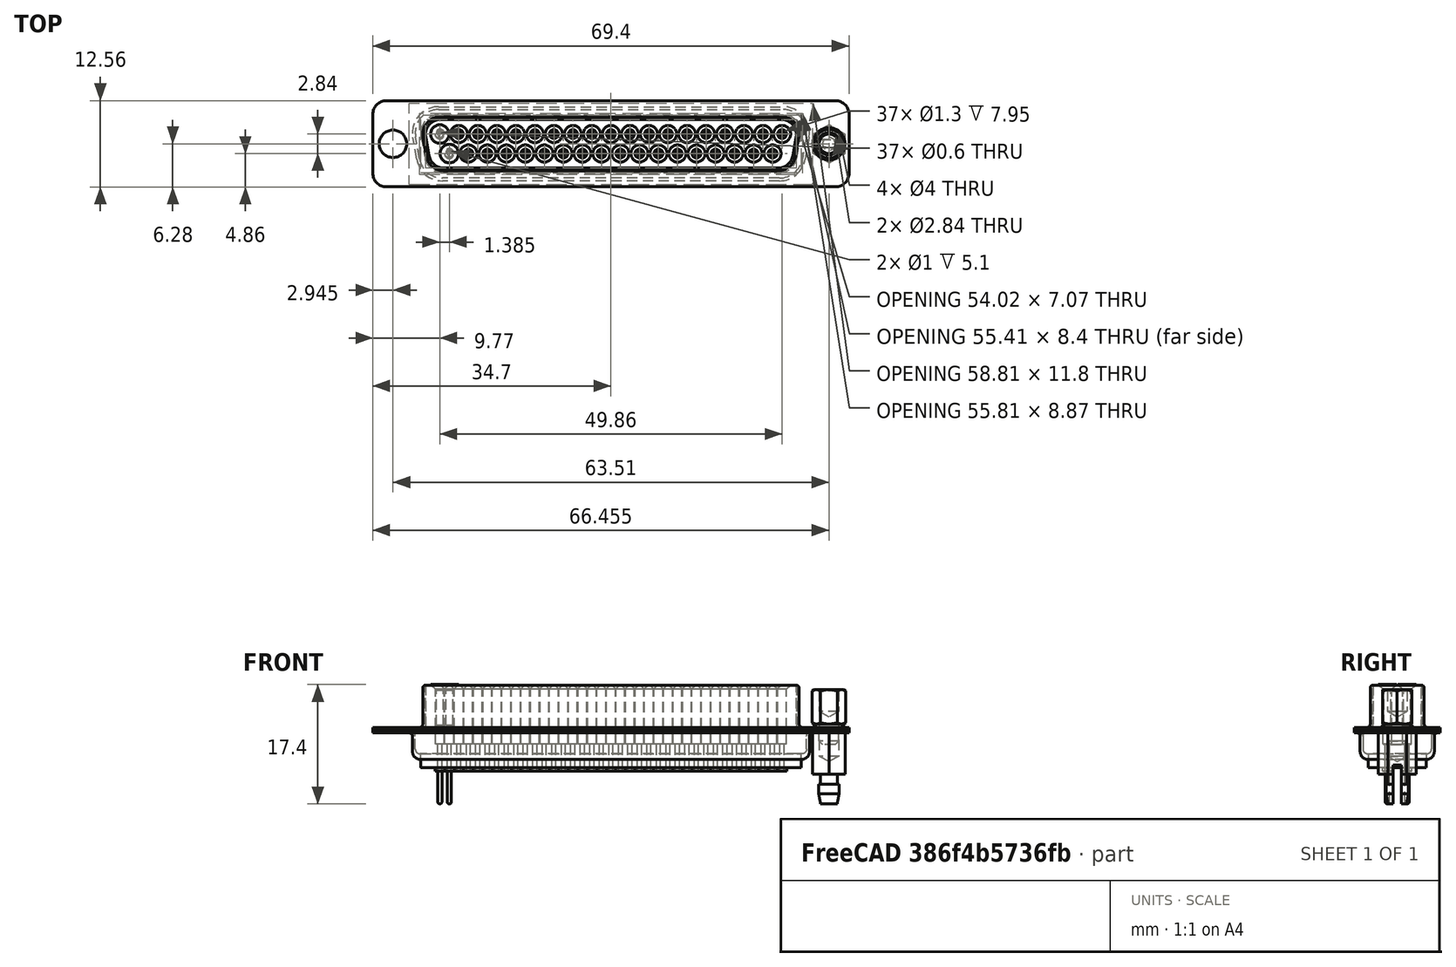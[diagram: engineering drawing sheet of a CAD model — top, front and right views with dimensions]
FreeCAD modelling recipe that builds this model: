
FCSTD DOCUMENT  (FreeCAD 1.0R39319 (Git))
Label: DB 37 Female
License: All rights reserved
LicenseURL: http://en.wikipedia.org/wiki/All_rights_reserved
objects: Sketcher::SketchObject×23, PartDesign::Body×13, PartDesign::Pad×9, PartDesign::Pocket×8, PartDesign::Fillet×8, PartDesign::Revolution×6, Part::FeaturePython×6, Part::MultiFuse×3, PartDesign::FeatureBase×2, PartDesign::Chamfer×1, Part::Cut×1
note: 163 computed .brp shape members not serialized (recipe doc carries the construction recipe); baked Part::Feature solids carry a one-line shape summary decoded from their .brp

FEATURE [Sketcher::SketchObject] Sketch
  ArcFitTolerance = 0
  AttachmentSupport = -> [XY_Plane]
  FullyConstrained = true
  MakeInternals = false
  MapMode = 5
  sketch-geometry (8):
    g0: LineSegment StartX=-32.7 StartY=6.275 StartZ=0 EndX=32.7 EndY=6.275 EndZ=0
    g1: LineSegment StartX=34.7 StartY=4.275 StartZ=0 EndX=34.7 EndY=-4.275 EndZ=0
    g2: LineSegment StartX=32.7 StartY=-6.275 StartZ=0 EndX=-32.7 EndY=-6.275 EndZ=0
    g3: LineSegment StartX=-34.7 StartY=-4.275 StartZ=0 EndX=-34.7 EndY=4.275 EndZ=0
    g4: ArcOfCircle CenterX=-32.7 CenterY=4.275 CenterZ=0 NormalX=0 NormalY=0 NormalZ=1 AngleXU=0 Radius=2 StartAngle=1.5708 EndAngle=3.14159
    g5: ArcOfCircle CenterX=-32.7 CenterY=-4.275 CenterZ=0 NormalX=0 NormalY=0 NormalZ=1 AngleXU=0 Radius=2 StartAngle=3.14159 EndAngle=4.71239
    g6: ArcOfCircle CenterX=32.7 CenterY=4.275 CenterZ=0 NormalX=0 NormalY=0 NormalZ=1 AngleXU=0 Radius=2 StartAngle=0 EndAngle=1.5708
    g7: ArcOfCircle CenterX=32.7 CenterY=-4.275 CenterZ=0 NormalX=0 NormalY=0 NormalZ=1 AngleXU=0 Radius=2 StartAngle=4.71239 EndAngle=6.28319
  constraints (19):
    c: Horizontal(g0)
    c: Horizontal(g2)
    c: Vertical(g1)
    c: Vertical(g3)
    c: Tangent(g0,g4) = 1.5708
    c: Tangent(g3,g4) = 1.5708
    c: Tangent(g3,g5) = 1.5708
    c: Tangent(g2,g5) = 1.5708
    c: Tangent(g0,g6) = 1.5708
    c: Tangent(g1,g6) = 1.5708
    c: Tangent(g1,g7) = 1.5708
    c: Tangent(g2,g7) = 1.5708
    c: Equal(g7,g6)
    c: Equal(g6,g4)
    c: Equal(g4,g5)
    c: Symmetric(g4,g7,g-1)
    c: Radius(g4) = 2
    c: DistanceY(g2,g0) = 12.55
    c: DistanceX(g3,g1) = 69.4
FEATURE [PartDesign::Pad] Pad
  Direction = (0,0,1)
  Length = 0.4
  Length2 = 10
  Profile = -> Sketch
  ReferenceAxis = -> Sketch [N_Axis]
  Suppressed = false
  Type = 0
FEATURE [Sketcher::SketchObject] Sketch001
  ArcFitTolerance = 0
  AttachmentSupport = -> [Pad]
  FullyConstrained = true
  MakeInternals = false
  MapMode = 5
  Placement = pos=(0,0,0.4) rot=(0,0,1;0rad)
  sketch-geometry (2):
    g0: Circle CenterX=-31.755 CenterY=0 CenterZ=0 NormalX=0 NormalY=0 NormalZ=1 AngleXU=0 Radius=2
    g1: Circle CenterX=31.755 CenterY=0 CenterZ=0 NormalX=0 NormalY=0 NormalZ=1 AngleXU=0 Radius=2
  constraints (5):
    c: PointOnObject(g0,g-1)
    c: Symmetric(g1,g0,g-2)
    c: Equal(g1,g0)
    c: DistanceX(g0,g1) = 63.51
    c: Diameter(g0) = 4
FEATURE [PartDesign::Pocket] Pocket
  BaseFeature = -> Pad
  Direction = (0,0,-1)
  Length = 5
  Length2 = 5
  Profile = -> Sketch001
  ReferenceAxis = -> Sketch001 [N_Axis]
  Suppressed = false
  Type = 0
FEATURE [Sketcher::SketchObject] Sketch002
  ArcFitTolerance = 0
  AttachmentSupport = -> [Pocket]
  FullyConstrained = true
  MakeInternals = false
  MapMode = 5
  Placement = pos=(0,0,0.4) rot=(0,0,1;0rad)
  sketch-geometry (10):
    g0: LineSegment StartX=-24.865 StartY=3.935 StartZ=0 EndX=24.865 EndY=3.935 EndZ=0
    g1: LineSegment StartX=27.3714 StartY=0.948231 StartZ=0 EndX=26.8814 EndY=-1.83177 EndZ=0
    g2: LineSegment StartX=24.375 StartY=-3.935 StartZ=0 EndX=-24.375 EndY=-3.935 EndZ=0
    g3: LineSegment StartX=-26.8814 StartY=-1.83177 StartZ=0 EndX=-27.3714 EndY=0.948231 EndZ=0
    g4: ArcOfCircle CenterX=-24.865 CenterY=1.39 CenterZ=0 NormalX=0 NormalY=0 NormalZ=1 AngleXU=0 Radius=2.545 StartAngle=1.5708 EndAngle=3.31606
    g5: ArcOfCircle CenterX=-24.375 CenterY=-1.39 CenterZ=0 NormalX=0 NormalY=0 NormalZ=1 AngleXU=0 Radius=2.545 StartAngle=3.31606 EndAngle=4.71239
    g6: ArcOfCircle CenterX=24.375 CenterY=-1.39 CenterZ=0 NormalX=0 NormalY=0 NormalZ=1 AngleXU=0 Radius=2.545 StartAngle=4.71239 EndAngle=6.10872
    g7: ArcOfCircle CenterX=24.865 CenterY=1.39 CenterZ=0 NormalX=0 NormalY=0 NormalZ=1 AngleXU=0 Radius=2.545 StartAngle=6.10872 EndAngle=7.85398
    g8: LineSegment [constr] StartX=-24.865 StartY=3.935 StartZ=0 EndX=-24.865 EndY=0 EndZ=0
    g9: LineSegment [constr] StartX=-24.375 StartY=-3.935 StartZ=0 EndX=-24.375 EndY=0 EndZ=0
  constraints (24):
    c: Tangent(g0,g4) = 1.5708
    c: Tangent(g3,g4) = 1.5708
    c: Tangent(g3,g5) = 1.5708
    c: Tangent(g2,g5) = 1.5708
    c: Tangent(g2,g6) = 1.5708
    c: Tangent(g1,g6) = 1.5708
    c: Tangent(g1,g7) = 1.5708
    c: Tangent(g0,g7) = 1.5708
    c: Symmetric(g4,g7,g-2)
    c: Equal(g4,g5)
    c: Equal(g5,g7)
    c: Equal(g7,g6)
    c: Symmetric(g5,g6,g-2)
    c: Coincident(g8,g0)
    c: PointOnObject(g8,g-1)
    c: Vertical(g8)
    c: Coincident(g9,g2)
    c: PointOnObject(g9,g-1)
    c: Vertical(g9)
    c: Equal(g9,g8)
    c: DistanceY(g2,g0) = 7.87
    c: DistanceX(g0,g0) = 49.73
    c: DistanceX(g2,g2) = 48.75
    c: Radius(g4) = 2.545
FEATURE [PartDesign::Pad] Pad001
  BaseFeature = -> Pocket
  Direction = (0,0,1)
  Length = 6.15
  Length2 = 10
  Profile = -> Sketch002
  ReferenceAxis = -> Sketch002 [N_Axis]
  Suppressed = false
  Type = 0
FEATURE [Sketcher::SketchObject] Sketch003
  ArcFitTolerance = 0
  AttachmentSupport = -> [Pad001]
  ExternalGeometry = -> [Pad001]
  FullyConstrained = true
  MakeInternals = false
  MapMode = 5
  Placement = pos=(0,0,6.55) rot=(0,0,1;0rad)
  sketch-geometry (8):
    g0: LineSegment StartX=-24.865 StartY=3.535 StartZ=0 EndX=24.865 EndY=3.535 EndZ=0
    g1: LineSegment StartX=26.9774 StartY=1.01766 StartZ=0 EndX=26.4874 EndY=-1.76234 EndZ=0
    g2: LineSegment StartX=24.375 StartY=-3.535 StartZ=0 EndX=-24.375 EndY=-3.535 EndZ=0
    g3: LineSegment StartX=-26.4874 StartY=-1.76234 StartZ=0 EndX=-26.9774 EndY=1.01766 EndZ=0
    g4: ArcOfCircle CenterX=-24.865 CenterY=1.39 CenterZ=0 NormalX=0 NormalY=0 NormalZ=1 AngleXU=0 Radius=2.145 StartAngle=1.5708 EndAngle=3.31606
    g5: ArcOfCircle CenterX=24.865 CenterY=1.39 CenterZ=0 NormalX=0 NormalY=0 NormalZ=1 AngleXU=0 Radius=2.145 StartAngle=6.10872 EndAngle=7.85398
    g6: ArcOfCircle CenterX=24.375 CenterY=-1.39 CenterZ=0 NormalX=0 NormalY=0 NormalZ=1 AngleXU=0 Radius=2.145 StartAngle=4.71239 EndAngle=6.10872
    g7: ArcOfCircle CenterX=-24.375 CenterY=-1.39 CenterZ=0 NormalX=0 NormalY=0 NormalZ=1 AngleXU=0 Radius=2.145 StartAngle=3.31606 EndAngle=4.71239
  constraints (16):
    c: Tangent(g0,g4) = 1.5708
    c: Tangent(g3,g4) = 1.5708
    c: Tangent(g0,g5) = 1.5708
    c: Tangent(g1,g5) = 1.5708
    c: Tangent(g2,g6) = 1.5708
    c: Tangent(g1,g6) = 1.5708
    c: Tangent(g3,g7) = 1.5708
    c: Tangent(g2,g7) = 1.5708
    c: Equal(g4,g7)
    c: Equal(g7,g5)
    c: Equal(g5,g6)
    c: Coincident(g6,g-6)
    c: Coincident(g5,g-5)
    c: Coincident(g4,g-3)
    c: Coincident(g7,g-4)
    c: DistanceY(g0,g-3) = 0.4
FEATURE [PartDesign::Pocket] Pocket001
  BaseFeature = -> Pad001
  Direction = (0,0,-1)
  Length = 5
  Length2 = 5
  Profile = -> Sketch003
  ReferenceAxis = -> Sketch003 [N_Axis]
  Suppressed = false
  Type = 1
FEATURE [PartDesign::Fillet] Fillet
  Base = -> Pocket001 [Edge33]
  BaseFeature = -> Pocket001
  Radius = 0.5
  SupportTransform = false
  Suppressed = false
  UseAllEdges = false
FEATURE [PartDesign::Fillet] Fillet001
  Base = -> Fillet [Edge61]
  BaseFeature = -> Fillet
  Radius = 0.39
  SupportTransform = false
  Suppressed = false
  UseAllEdges = false
FEATURE [PartDesign::Fillet] Fillet002
  Base = -> Fillet001 [Edge80]
  BaseFeature = -> Fillet001
  Radius = 0.9
  SupportTransform = false
  Suppressed = false
  UseAllEdges = false
FEATURE [PartDesign::Body] Body
  AllowCompound = false
  Group = -> [Sketch,Pad,Sketch001,Pocket,Sketch002,Sketch003,Pad001,Pocket001,Fillet,Fillet001,Fillet002]
  Origin = -> Origin
  Tip = -> Fillet002
FEATURE [Sketcher::SketchObject] Sketch004
  ArcFitTolerance = 0
  AttachmentSupport = -> [XY_Plane001]
  FullyConstrained = true
  MakeInternals = false
  MapMode = 5
  sketch-geometry (8):
    g0: LineSegment StartX=-32.7 StartY=6.275 StartZ=0 EndX=32.7 EndY=6.275 EndZ=0
    g1: LineSegment StartX=34.7 StartY=4.275 StartZ=0 EndX=34.7 EndY=-4.275 EndZ=0
    g2: LineSegment StartX=32.7 StartY=-6.275 StartZ=0 EndX=-32.7 EndY=-6.275 EndZ=0
    g3: LineSegment StartX=-34.7 StartY=-4.275 StartZ=0 EndX=-34.7 EndY=4.275 EndZ=0
    g4: ArcOfCircle CenterX=-32.7 CenterY=4.275 CenterZ=0 NormalX=0 NormalY=0 NormalZ=1 AngleXU=0 Radius=2 StartAngle=1.5708 EndAngle=3.14159
    g5: ArcOfCircle CenterX=-32.7 CenterY=-4.275 CenterZ=0 NormalX=0 NormalY=0 NormalZ=1 AngleXU=0 Radius=2 StartAngle=3.14159 EndAngle=4.71239
    g6: ArcOfCircle CenterX=32.7 CenterY=4.275 CenterZ=0 NormalX=0 NormalY=0 NormalZ=1 AngleXU=0 Radius=2 StartAngle=0 EndAngle=1.5708
    g7: ArcOfCircle CenterX=32.7 CenterY=-4.275 CenterZ=0 NormalX=0 NormalY=0 NormalZ=1 AngleXU=0 Radius=2 StartAngle=4.71239 EndAngle=6.28319
  constraints (19):
    c: Horizontal(g0)
    c: Horizontal(g2)
    c: Vertical(g1)
    c: Vertical(g3)
    c: Tangent(g0,g4) = 1.5708
    c: Tangent(g3,g4) = 1.5708
    c: Tangent(g3,g5) = 1.5708
    c: Tangent(g2,g5) = 1.5708
    c: Tangent(g0,g6) = 1.5708
    c: Tangent(g1,g6) = 1.5708
    c: Tangent(g1,g7) = 1.5708
    c: Tangent(g2,g7) = 1.5708
    c: Equal(g7,g6)
    c: Equal(g6,g4)
    c: Equal(g4,g5)
    c: Symmetric(g4,g7,g-1)
    c: Radius(g4) = 2
    c: DistanceY(g2,g0) = 12.55
    c: DistanceX(g3,g1) = 69.4
FEATURE [PartDesign::Pad] Pad002
  Direction = (0,0,1)
  Length = 0.4
  Length2 = 10
  Profile = -> Sketch004
  ReferenceAxis = -> Sketch004 [N_Axis]
  Suppressed = false
  Type = 0
FEATURE [Sketcher::SketchObject] Sketch005
  ArcFitTolerance = 0
  AttachmentSupport = -> [Pad002]
  FullyConstrained = true
  MakeInternals = false
  MapMode = 5
  Placement = pos=(0,0,0.4) rot=(0,0,1;0rad)
  sketch-geometry (2):
    g0: Circle CenterX=-31.755 CenterY=0 CenterZ=0 NormalX=0 NormalY=0 NormalZ=1 AngleXU=0 Radius=2
    g1: Circle CenterX=31.755 CenterY=0 CenterZ=0 NormalX=0 NormalY=0 NormalZ=1 AngleXU=0 Radius=2
  constraints (5):
    c: PointOnObject(g0,g-1)
    c: Symmetric(g1,g0,g-2)
    c: Equal(g1,g0)
    c: DistanceX(g0,g1) = 63.51
    c: Diameter(g0) = 4
FEATURE [PartDesign::Pocket] Pocket002
  BaseFeature = -> Pad002
  Direction = (0,0,-1)
  Length = 5
  Length2 = 5
  Profile = -> Sketch005
  ReferenceAxis = -> Sketch005 [N_Axis]
  Suppressed = false
  Type = 0
FEATURE [Sketcher::SketchObject] Sketch006
  ArcFitTolerance = 0
  AttachmentSupport = -> [Pocket002]
  FullyConstrained = true
  MakeInternals = false
  MapMode = 5
  Placement = pos=(0,0,0.4) rot=(0,0,1;0rad)
  sketch-geometry (10):
    g0: LineSegment StartX=-25.11 StartY=5.4 StartZ=0 EndX=25.11 EndY=5.4 EndZ=0
    g1: LineSegment StartX=28.8521 StartY=0.939282 StartZ=0 EndX=28.2871 EndY=-2.26072 EndZ=0
    g2: LineSegment StartX=24.545 StartY=-5.4 StartZ=0 EndX=-24.545 EndY=-5.4 EndZ=0
    g3: LineSegment StartX=-28.2871 StartY=-2.26072 StartZ=0 EndX=-28.8521 EndY=0.939282 EndZ=0
    g4: ArcOfCircle CenterX=-25.11 CenterY=1.6 CenterZ=0 NormalX=0 NormalY=0 NormalZ=1 AngleXU=0 Radius=3.8 StartAngle=1.5708 EndAngle=3.31635
    g5: ArcOfCircle CenterX=-24.545 CenterY=-1.6 CenterZ=0 NormalX=0 NormalY=0 NormalZ=1 AngleXU=0 Radius=3.8 StartAngle=3.31635 EndAngle=4.71239
    g6: ArcOfCircle CenterX=24.545 CenterY=-1.6 CenterZ=0 NormalX=0 NormalY=0 NormalZ=1 AngleXU=0 Radius=3.8 StartAngle=4.71239 EndAngle=6.10842
    g7: ArcOfCircle CenterX=25.11 CenterY=1.6 CenterZ=0 NormalX=0 NormalY=0 NormalZ=1 AngleXU=0 Radius=3.8 StartAngle=6.10842 EndAngle=7.85398
    g8: LineSegment [constr] StartX=-25.11 StartY=5.4 StartZ=0 EndX=-25.11 EndY=0 EndZ=0
    g9: LineSegment [constr] StartX=-24.545 StartY=-5.4 StartZ=0 EndX=-24.545 EndY=0 EndZ=0
  constraints (24):
    c: Tangent(g0,g4) = 1.5708
    c: Tangent(g3,g4) = 1.5708
    c: Tangent(g3,g5) = 1.5708
    c: Tangent(g2,g5) = 1.5708
    c: Tangent(g2,g6) = 1.5708
    c: Tangent(g1,g6) = 1.5708
    c: Tangent(g1,g7) = 1.5708
    c: Tangent(g0,g7) = 1.5708
    c: Symmetric(g4,g7,g-2)
    c: Equal(g4,g5)
    c: Equal(g5,g7)
    c: Equal(g7,g6)
    c: Symmetric(g5,g6,g-2)
    c: DistanceX(g0,g0) = 50.22
    c: DistanceX(g2,g2) = 49.09
    c: Coincident(g8,g0)
    c: PointOnObject(g8,g-1)
    c: Vertical(g8)
    c: Coincident(g9,g2)
    c: PointOnObject(g9,g-1)
    c: Vertical(g9)
    c: Equal(g9,g8)
    c: DistanceY(g2,g0) = 10.8
    c: Radius(g4) = 3.8
FEATURE [PartDesign::Pad] Pad003
  BaseFeature = -> Pocket002
  Direction = (0,0,1)
  Length = 3.85
  Length2 = 10
  Profile = -> Sketch006
  ReferenceAxis = -> Sketch006 [N_Axis]
  Suppressed = false
  Type = 0
FEATURE [Sketcher::SketchObject] Sketch007
  ArcFitTolerance = 0
  AttachmentSupport = -> [Pad003]
  ExternalGeometry = -> [Pad003]
  FullyConstrained = true
  MakeInternals = false
  MapMode = 5
  Placement = pos=(0,0,4.25) rot=(0,0,1;0rad)
  sketch-geometry (8):
    g0: LineSegment StartX=-25.11 StartY=4.2 StartZ=0 EndX=25.11 EndY=4.2 EndZ=0
    g1: LineSegment StartX=27.6704 StartY=1.14793 StartZ=0 EndX=27.1054 EndY=-2.05207 EndZ=0
    g2: LineSegment StartX=24.545 StartY=-4.2 StartZ=0 EndX=-24.545 EndY=-4.2 EndZ=0
    g3: LineSegment StartX=-27.1054 StartY=-2.05207 StartZ=0 EndX=-27.6704 EndY=1.14793 EndZ=0
    g4: ArcOfCircle CenterX=-25.11 CenterY=1.6 CenterZ=0 NormalX=0 NormalY=0 NormalZ=1 AngleXU=0 Radius=2.6 StartAngle=1.5708 EndAngle=3.31635
    g5: ArcOfCircle CenterX=25.11 CenterY=1.6 CenterZ=0 NormalX=0 NormalY=0 NormalZ=1 AngleXU=0 Radius=2.6 StartAngle=6.10842 EndAngle=7.85398
    g6: ArcOfCircle CenterX=24.545 CenterY=-1.6 CenterZ=0 NormalX=0 NormalY=0 NormalZ=1 AngleXU=0 Radius=2.6 StartAngle=4.71239 EndAngle=6.10842
    g7: ArcOfCircle CenterX=-24.545 CenterY=-1.6 CenterZ=0 NormalX=0 NormalY=0 NormalZ=1 AngleXU=0 Radius=2.6 StartAngle=3.31635 EndAngle=4.71239
  constraints (20):
    c: Tangent(g0,g4) = 1.5708
    c: Tangent(g3,g4) = 1.5708
    c: Tangent(g0,g5) = 1.5708
    c: Tangent(g1,g5) = 1.5708
    c: Tangent(g2,g6) = 1.5708
    c: Tangent(g1,g6) = 1.5708
    c: Tangent(g3,g7) = 1.5708
    c: Tangent(g2,g7) = 1.5708
    c: Equal(g4,g7)
    c: Equal(g7,g5)
    c: Equal(g5,g6)
    c: Coincident(g6,g-6)
    c: Coincident(g5,g-5)
    c: Coincident(g4,g-3)
    c: Coincident(g7,g-4)
    c: DistanceY(g0,g-3) = 1.2
    c: Radius(g4) = 2.6
    c: DistanceY(g2,g0) = 8.4
    c: DistanceX(g0,g0) = 50.22
    c: DistanceX(g2,g2) = 49.09
FEATURE [PartDesign::Pocket] Pocket003
  BaseFeature = -> Pad003
  Direction = (0,0,-1)
  Length = 5
  Length2 = 5
  Profile = -> Sketch007
  ReferenceAxis = -> Sketch007 [N_Axis]
  Suppressed = false
  Type = 1
FEATURE [Sketcher::SketchObject] Sketch008
  ArcFitTolerance = 0
  AttachmentSupport = -> [Pocket003]
  ExternalGeometry = -> [Pocket003]
  FullyConstrained = true
  MakeInternals = false
  MapMode = 5
  Placement = pos=(0,0,0) rot=(1,0,0;3.14159rad)
  sketch-geometry (8):
    g0: LineSegment StartX=-24.545 StartY=5 StartZ=0 EndX=24.545 EndY=5 EndZ=0
    g1: LineSegment StartX=27.8932 StartY=2.19117 StartZ=0 EndX=28.4582 EndY=-1.00883 EndZ=0
    g2: LineSegment StartX=25.11 StartY=-5 StartZ=0 EndX=-25.11 EndY=-5 EndZ=0
    g3: LineSegment StartX=-28.4582 StartY=-1.00883 StartZ=0 EndX=-27.8932 EndY=2.19117 EndZ=0
    g4: ArcOfCircle CenterX=-24.545 CenterY=1.6 CenterZ=0 NormalX=0 NormalY=0 NormalZ=1 AngleXU=0 Radius=3.4 StartAngle=1.5708 EndAngle=2.96683
    g5: ArcOfCircle CenterX=-25.11 CenterY=-1.6 CenterZ=0 NormalX=0 NormalY=0 NormalZ=1 AngleXU=0 Radius=3.4 StartAngle=2.96683 EndAngle=4.71239
    g6: ArcOfCircle CenterX=25.11 CenterY=-1.6 CenterZ=0 NormalX=0 NormalY=0 NormalZ=1 AngleXU=0 Radius=3.4 StartAngle=4.71239 EndAngle=6.45795
    g7: ArcOfCircle CenterX=24.545 CenterY=1.6 CenterZ=0 NormalX=0 NormalY=0 NormalZ=1 AngleXU=0 Radius=3.4 StartAngle=0.174761 EndAngle=1.5708
  constraints (16):
    c: Tangent(g0,g4) = 1.5708
    c: Tangent(g3,g4) = 1.5708
    c: Tangent(g3,g5) = 1.5708
    c: Tangent(g2,g5) = 1.5708
    c: Tangent(g2,g6) = 1.5708
    c: Tangent(g1,g6) = 1.5708
    c: Tangent(g1,g7) = 1.5708
    c: Tangent(g0,g7) = 1.5708
    c: Coincident(g-3,g4)
    c: Coincident(g5,g-4)
    c: Coincident(g-6,g7)
    c: Coincident(g-5,g6)
    c: Equal(g5,g4)
    c: Equal(g4,g7)
    c: Equal(g7,g6)
    c: DistanceY(g-3,g0) = 0.8
FEATURE [PartDesign::Pocket] Pocket004
  BaseFeature = -> Pocket003
  Direction = (0,0,1)
  Length = 3.45
  Length2 = 5
  Profile = -> Sketch008
  ReferenceAxis = -> Sketch008 [N_Axis]
  Suppressed = false
  Type = 0
FEATURE [PartDesign::Fillet] Fillet003
  Base = -> Pocket004 [Edge58]
  BaseFeature = -> Pocket004
  Radius = 0.7
  SupportTransform = false
  Suppressed = false
  UseAllEdges = false
FEATURE [PartDesign::Fillet] Fillet004
  Base = -> Fillet003 [Edge99]
  BaseFeature = -> Fillet003
  Radius = 0.5
  SupportTransform = false
  Suppressed = false
  UseAllEdges = false
FEATURE [PartDesign::Fillet] Fillet005
  Base = -> Fillet004 [Edge56]
  BaseFeature = -> Fillet004
  Radius = 1.1
  SupportTransform = false
  Suppressed = false
  UseAllEdges = false
FEATURE [PartDesign::Fillet] Fillet006
  Base = -> Fillet005 [Edge125]
  BaseFeature = -> Fillet005
  Radius = 0.9
  SupportTransform = false
  Suppressed = false
  UseAllEdges = false
FEATURE [PartDesign::Body] Body001
  AllowCompound = false
  Group = -> [Sketch004,Pad002,Sketch005,Pocket002,Sketch006,Sketch007,Pad003,Pocket003,Sketch008,Pocket004,Fillet003,Fillet004,Fillet005,Fillet006]
  Origin = -> Origin001
  Placement = pos=(0,0,0) rot=(0,1,0;3.14159rad)
  Tip = -> Fillet006
FEATURE [Sketcher::SketchObject] Sketch009
  ArcFitTolerance = 0
  AttachmentSupport = -> [XZ_Plane002]
  FullyConstrained = true
  MakeInternals = false
  MapMode = 5
  Placement = pos=(0,0,0) rot=(1,0,0;1.5708rad)
  sketch-geometry (14):
    g0: LineSegment StartX=1.4224 StartY=0.5 StartZ=0 EndX=1.4224 EndY=-4.17878 EndZ=0
    g1: LineSegment StartX=1.4224 StartY=-4.17878 StartZ=0 EndX=0 EndY=-5 EndZ=0
    g2: LineSegment StartX=0 StartY=-5 StartZ=0 EndX=0 EndY=-11.1 EndZ=0
    g3: LineSegment StartX=0 StartY=-11.1 StartZ=0 EndX=1.35 EndY=-11.1 EndZ=0
    g4: LineSegment StartX=1.35 StartY=-11.1 StartZ=0 EndX=1.6 EndY=-9.7 EndZ=0
    g5: LineSegment StartX=1.6 StartY=-9.7 StartZ=0 EndX=1.6 EndY=-8.3 EndZ=0
    g6: LineSegment StartX=1.6 StartY=-8.3 StartZ=0 EndX=1.4 EndY=-8.3 EndZ=0
    g7: LineSegment StartX=1.4 StartY=-8.3 StartZ=0 EndX=1.4 EndY=-6.8 EndZ=0
    g8: LineSegment StartX=1.4 StartY=-6.8 StartZ=0 EndX=4 EndY=-6.8 EndZ=0
    g9: LineSegment StartX=4 StartY=-6.8 StartZ=0 EndX=4 EndY=-0.8 EndZ=0
    g10: LineSegment StartX=4 StartY=-0.8 StartZ=0 EndX=2 EndY=-0.8 EndZ=0
    g11: LineSegment StartX=2 StartY=-0.8 StartZ=0 EndX=2 EndY=0 EndZ=0
    g12: LineSegment StartX=2 StartY=0 StartZ=0 EndX=2.35 EndY=-9.64e-14 EndZ=0
    g13: ArcOfCircle CenterX=1.4224 CenterY=-0.610442 CenterZ=0 NormalX=0 NormalY=0 NormalZ=1 AngleXU=0 Radius=1.11044 StartAngle=0.582039 EndAngle=1.5708
  constraints (43):
    c: Vertical(g0)
    c: Coincident(g0,g1)
    c: Coincident(g1,g2)
    c: Vertical(g2)
    c: Coincident(g2,g3)
    c: Coincident(g3,g4)
    c: Coincident(g4,g5)
    c: Vertical(g5)
    c: Coincident(g5,g6)
    c: Horizontal(g6)
    c: Coincident(g6,g7)
    c: Vertical(g7)
    c: Coincident(g7,g8)
    c: Coincident(g8,g9)
    c: Vertical(g9)
    c: Coincident(g9,g10)
    c: Horizontal(g10)
    c: Coincident(g10,g11)
    c: PointOnObject(g11,g-1)
    c: Vertical(g11)
    c: Coincident(g11,g12)
    c: PointOnObject(g12,g-1)
    c: Coincident(g13,g12)
    c: Coincident(g13,g0)
    c: PointOnObject(g13,g0)
    c: DistanceX(g-1,g11) = 2
    c: DistanceX(g-1,g0) = 1.4224
    c: DistanceY(g10,g11) = 0.8
    c: Horizontal(g8)
    c: DistanceY(g9,g9) = 6
    c: DistanceY(g3,g9) = 10.3
    c: Horizontal(g3)
    c: DistanceX(g2,g4) = 1.6
    c: PointOnObject(g1,g-2)
    c: DistanceY(g5,g8) = 1.5
    c: DistanceX(g2,g6) = 1.4
    c: DistanceX(g3,g4) = 0.25
    c: DistanceY(g4,g4) = 1.4
    c: DistanceY(g1,g-1) = 5
    c: Angle(g1,g-2) = 1.0472
    c: DistanceX(g12,g12) = 0.35
    c: DistanceY(g11,g0) = 0.5
    c: DistanceX(g-1,g9) = 4
FEATURE [PartDesign::Revolution] Revolution
  Angle = 360
  Angle2 = 60
  Axis = (0,2e-16,1)
  Base = (0,0,0)
  Placement = pos=(0,0,0) rot=(1,0,0;1.5708rad)
  Profile = -> Sketch009
  ReferenceAxis = -> Sketch009 [V_Axis]
  Reversed = true
  Suppressed = false
  Type = 0
FEATURE [Sketcher::SketchObject] Sketch010
  ArcFitTolerance = 0
  AttachmentSupport = -> [Revolution]
  FullyConstrained = false
  MakeInternals = false
  MapMode = 5
  Placement = pos=(0,-2e-16,-0.8) rot=(0,0,1;3.14159rad)
  sketch-geometry (8):
    g0: LineSegment StartX=0 StartY=2.74241 StartZ=0 EndX=-2.375 EndY=1.37121 EndZ=0
    g1: LineSegment StartX=-2.375 StartY=1.37121 StartZ=0 EndX=-2.375 EndY=-1.37121 EndZ=0
    g2: LineSegment StartX=-2.375 StartY=-1.37121 StartZ=0 EndX=-7.545e-13 EndY=-2.74241 EndZ=0
    g3: LineSegment StartX=-7.545e-13 StartY=-2.74241 StartZ=0 EndX=2.375 EndY=-1.37121 EndZ=0
    g4: LineSegment StartX=2.375 StartY=-1.37121 StartZ=0 EndX=2.375 EndY=1.37121 EndZ=0
    g5: LineSegment StartX=2.375 StartY=1.37121 StartZ=0 EndX=0 EndY=2.74241 EndZ=0
    g6: Circle [constr] CenterX=0 CenterY=0 CenterZ=0 NormalX=0 NormalY=0 NormalZ=1 AngleXU=0 Radius=2.74241
    g7: Circle CenterX=0 CenterY=0 CenterZ=0 NormalX=0 NormalY=0 NormalZ=1 AngleXU=0 Radius=4.67961
  constraints (17):
    c: Coincident(g0,g1)
    c: Coincident(g1,g2)
    c: Coincident(g2,g3)
    c: Coincident(g3,g4)
    c: Coincident(g4,g5)
    c: Coincident(g5,g0)
    c: Equal(g0, g1-g5) x5
    c: PointOnObject(g0,g6)
    c: PointOnObject(g1,g6)
    c: PointOnObject(g2,g6)
    c: PointOnObject(g3,g6)
    c: PointOnObject(g4,g6)
    c: PointOnObject(g5,g6)
    c: Coincident(g6,g-1)
    c: PointOnObject(g5,g-2)
    c: DistanceX(g0,g4) = 4.75
    c: Coincident(g7,g6)
FEATURE [PartDesign::Pocket] Pocket005
  BaseFeature = -> Revolution
  Direction = (0,0,-1)
  Length = 5
  Length2 = 5
  Placement = pos=(0,0,0) rot=(1,0,0;1.5708rad)
  Profile = -> Sketch010
  ReferenceAxis = -> Sketch010 [N_Axis]
  Suppressed = false
  Type = 1
FEATURE [Sketcher::SketchObject] Sketch011
  ArcFitTolerance = 0
  AttachmentSupport = -> [YZ_Plane002]
  FullyConstrained = true
  MakeInternals = false
  MapMode = 5
  Placement = pos=(0,0,0) rot=(0.57735,0.57735,0.57735;2.0944rad)
  sketch-geometry (4):
    g0: LineSegment StartX=-0.6 StartY=-5.5 StartZ=0 EndX=0.6 EndY=-5.5 EndZ=0
    g1: LineSegment StartX=0.6 StartY=-5.5 StartZ=0 EndX=0.6 EndY=-11.5 EndZ=0
    g2: LineSegment StartX=0.6 StartY=-11.5 StartZ=0 EndX=-0.6 EndY=-11.5 EndZ=0
    g3: LineSegment StartX=-0.6 StartY=-11.5 StartZ=0 EndX=-0.6 EndY=-5.5 EndZ=0
  constraints (11):
    c: Coincident(g0,g1)
    c: Coincident(g1,g2)
    c: Coincident(g2,g3)
    c: Coincident(g3,g0)
    c: Horizontal(g0)
    c: Vertical(g1)
    c: Vertical(g3)
    c: Symmetric(g1,g2,g-2)
    c: DistanceX(g2,g2) = 1.2
    c: DistanceY(g0,g-1) = 5.5
    c: DistanceY(g3,g3) = 6
FEATURE [PartDesign::Pocket] Pocket006
  BaseFeature = -> Pocket005
  Direction = (-1,0,0)
  Length = 5
  Length2 = 5
  Midplane = true
  Placement = pos=(0,0,0) rot=(1,0,0;1.5708rad)
  Profile = -> Sketch011
  ReferenceAxis = -> Sketch011 [N_Axis]
  Suppressed = false
  Type = 1
FEATURE [PartDesign::Body] Body002
  AllowCompound = false
  Group = -> [Sketch009,Revolution,Sketch010,Pocket005,Sketch011,Pocket006]
  Origin = -> Origin002
  Placement = pos=(-31.755,0,0.4) rot=(0,0,1;0rad)
  Tip = -> Pocket006
FEATURE [PartDesign::FeatureBase] Clone
  BaseFeature = -> Body002
  Suppressed = false
FEATURE [PartDesign::Body] Body003
  AllowCompound = false
  BaseFeature = -> Body002
  Group = -> [Clone]
  Origin = -> Origin003
  Placement = pos=(31.755,0,0.4) rot=(0,0,1;0rad)
  Tip = -> Clone
FEATURE [Sketcher::SketchObject] Sketch012
  ArcFitTolerance = 0
  AttachmentSupport = -> [XZ_Plane004]
  FullyConstrained = true
  MakeInternals = false
  MapMode = 5
  Placement = pos=(0,0,0) rot=(1,0,0;1.5708rad)
  sketch-geometry (11):
    g0: LineSegment StartX=1.4224 StartY=5 StartZ=0 EndX=1.4224 EndY=1.82122 EndZ=0
    g1: LineSegment StartX=1.4224 StartY=1.82122 StartZ=0 EndX=0 EndY=1 EndZ=0
    g2: LineSegment StartX=0 StartY=1 StartZ=0 EndX=0 EndY=-3 EndZ=0
    g3: LineSegment StartX=0 StartY=-3 StartZ=0 EndX=0.9224 EndY=-3 EndZ=0
    g4: LineSegment StartX=0.9224 StartY=-3 StartZ=0 EndX=1.4224 EndY=-2.5 EndZ=0
    g5: LineSegment StartX=1.4224 StartY=-2.5 StartZ=0 EndX=1.4224 EndY=0 EndZ=0
    g6: LineSegment StartX=1.4224 StartY=0 StartZ=0 EndX=2.1 EndY=0 EndZ=0
    g7: LineSegment StartX=2.1 StartY=5 StartZ=0 EndX=1.4224 EndY=5 EndZ=0
    g8: LineSegment StartX=2.1 StartY=5 StartZ=0 EndX=3.1 EndY=4.42265 EndZ=0
    g9: LineSegment StartX=3.1 StartY=4.42265 StartZ=0 EndX=3.1 EndY=0.57735 EndZ=0
    g10: LineSegment StartX=3.1 StartY=0.57735 StartZ=0 EndX=2.1 EndY=0 EndZ=0
  constraints (33):
    c: Vertical(g0)
    c: Coincident(g0,g1)
    c: Coincident(g1,g2)
    c: Vertical(g2)
    c: Coincident(g2,g3)
    c: Horizontal(g3)
    c: Coincident(g3,g4)
    c: Coincident(g4,g5)
    c: Vertical(g5)
    c: Coincident(g5,g6)
    c: Horizontal(g6)
    c: Coincident(g7,g0)
    c: PointOnObject(g5,g-1)
    c: Angle(g5,g4) = 2.35619
    c: PointOnObject(g1,g-2)
    c: Angle(g-2,g1) = 2.0944
    c: Vertical(g0,g5)
    c: DistanceX(g2,g4) = 1.4224
    c: Horizontal(g7)
    c: Vertical(g7,g6)
    c: Coincident(g7,g8)
    c: Coincident(g8,g9)
    c: Vertical(g9)
    c: Coincident(g9,g10)
    c: Coincident(g10,g6)
    c: Equal(g8,g10)
    c: Angle(g8,g10) = 1.0472
    c: DistanceX(g-1,g7) = 2.1
    c: DistanceY(g6,g7) = 5
    c: DistanceY(g1,g0) = 4
    c: DistanceX(g8,g8) = 1
    c: DistanceY(g4,g4) = 0.5
    c: DistanceY(g2,g-1) = 3
FEATURE [PartDesign::Revolution] Revolution001
  Angle = 360
  Angle2 = 60
  Axis = (0,2e-16,1)
  Base = (0,0,0)
  Placement = pos=(0,0,0) rot=(1,0,0;1.5708rad)
  Profile = -> Sketch012
  ReferenceAxis = -> Sketch012 [V_Axis]
  Reversed = true
  Suppressed = false
  Type = 0
FEATURE [Sketcher::SketchObject] Sketch013
  ArcFitTolerance = 0
  AttachmentSupport = -> [Revolution001]
  FullyConstrained = false
  MakeInternals = false
  MapMode = 5
  Placement = pos=(0,1.1e-15,5) rot=(0,0,1;3.14159rad)
  sketch-geometry (8):
    g0: LineSegment StartX=2.42487 StartY=0 StartZ=0 EndX=1.21244 EndY=2.1 EndZ=0
    g1: LineSegment StartX=1.21244 StartY=2.1 StartZ=0 EndX=-1.21244 EndY=2.1 EndZ=0
    g2: LineSegment StartX=-1.21244 StartY=2.1 StartZ=0 EndX=-2.42487 EndY=1.847e-12 EndZ=0
    g3: LineSegment StartX=-2.42487 StartY=1.847e-12 StartZ=0 EndX=-1.21244 EndY=-2.1 EndZ=0
    g4: LineSegment StartX=-1.21244 StartY=-2.1 StartZ=0 EndX=1.21244 EndY=-2.1 EndZ=0
    g5: LineSegment StartX=1.21244 StartY=-2.1 StartZ=0 EndX=2.42487 EndY=0 EndZ=0
    g6: Circle [constr] CenterX=0 CenterY=0 CenterZ=0 NormalX=0 NormalY=0 NormalZ=1 AngleXU=0 Radius=2.42487
    g7: Circle CenterX=0 CenterY=0 CenterZ=0 NormalX=0 NormalY=0 NormalZ=1 AngleXU=0 Radius=3.63045
  constraints (17):
    c: Coincident(g0,g1)
    c: Coincident(g1,g2)
    c: Coincident(g2,g3)
    c: Coincident(g3,g4)
    c: Coincident(g4,g5)
    c: Coincident(g5,g0)
    c: Equal(g0, g1-g5) x5
    c: PointOnObject(g0,g6)
    c: PointOnObject(g1,g6)
    c: PointOnObject(g2,g6)
    c: PointOnObject(g3,g6)
    c: PointOnObject(g4,g6)
    c: PointOnObject(g5,g6)
    c: Coincident(g6,g-1)
    c: PointOnObject(g5,g-1)
    c: DistanceY(g4,g0) = 4.2
    c: Coincident(g7,g6)
FEATURE [PartDesign::Pocket] Pocket007
  BaseFeature = -> Revolution001
  Direction = (0,0,-1)
  Length = 5
  Length2 = 5
  Placement = pos=(0,0,0) rot=(1,0,0;1.5708rad)
  Profile = -> Sketch013
  ReferenceAxis = -> Sketch013 [N_Axis]
  Suppressed = false
  Type = 1
FEATURE [PartDesign::Chamfer] Chamfer
  Angle = 45
  Base = -> Pocket007 [Edge1]
  BaseFeature = -> Pocket007
  ChamferType = 0
  FlipDirection = false
  Placement = pos=(0,0,0) rot=(1,0,0;1.5708rad)
  Size = 0.2
  Size2 = 1
  SupportTransform = false
  Suppressed = false
  UseAllEdges = false
FEATURE [PartDesign::Body] Body004
  AllowCompound = false
  Group = -> [Sketch012,Revolution001,Sketch013,Pocket007,Chamfer]
  Origin = -> Origin004
  Placement = pos=(-31.755,1e-16,0.9) rot=(0,0,1;0rad)
  Tip = -> Chamfer
FEATURE [PartDesign::FeatureBase] Clone001
  BaseFeature = -> Body004
  Suppressed = false
FEATURE [PartDesign::Body] Body005
  AllowCompound = false
  BaseFeature = -> Body004
  Group = -> [Clone001]
  Origin = -> Origin005
  Placement = pos=(31.755,1e-16,0.9) rot=(0,0,1;0rad)
  Tip = -> Clone001
FEATURE [Sketcher::SketchObject] Sketch014
  ArcFitTolerance = 0
  AttachmentSupport = -> [XY_Plane006]
  FullyConstrained = true
  MakeInternals = false
  MapMode = 5
  sketch-geometry (10):
    g0: LineSegment StartX=-25.11 StartY=5 StartZ=0 EndX=25.11 EndY=5 EndZ=0
    g1: LineSegment StartX=28.4582 StartY=1.00883 StartZ=0 EndX=27.8932 EndY=-2.19117 EndZ=0
    g2: LineSegment StartX=24.545 StartY=-5 StartZ=0 EndX=-24.545 EndY=-5 EndZ=0
    g3: LineSegment StartX=-27.8932 StartY=-2.19117 StartZ=0 EndX=-28.4582 EndY=1.00883 EndZ=0
    g4: ArcOfCircle CenterX=-25.11 CenterY=1.6 CenterZ=0 NormalX=0 NormalY=0 NormalZ=1 AngleXU=0 Radius=3.4 StartAngle=1.5708 EndAngle=3.31635
    g5: ArcOfCircle CenterX=25.11 CenterY=1.6 CenterZ=0 NormalX=0 NormalY=0 NormalZ=1 AngleXU=0 Radius=3.4 StartAngle=6.10842 EndAngle=7.85398
    g6: ArcOfCircle CenterX=24.545 CenterY=-1.6 CenterZ=0 NormalX=0 NormalY=0 NormalZ=1 AngleXU=0 Radius=3.4 StartAngle=4.71239 EndAngle=6.10842
    g7: ArcOfCircle CenterX=-24.545 CenterY=-1.6 CenterZ=0 NormalX=0 NormalY=0 NormalZ=1 AngleXU=0 Radius=3.4 StartAngle=3.31635 EndAngle=4.71239
    g8: LineSegment [constr] StartX=-25.11 StartY=5 StartZ=0 EndX=-25.11 EndY=0 EndZ=0
    g9: LineSegment [constr] StartX=-24.545 StartY=-5 StartZ=0 EndX=-24.545 EndY=0 EndZ=0
  constraints (24):
    c: Tangent(g0,g4) = 1.5708
    c: Tangent(g3,g4) = 1.5708
    c: Tangent(g0,g5) = 1.5708
    c: Tangent(g1,g5) = 1.5708
    c: Tangent(g1,g6) = 1.5708
    c: Tangent(g2,g6) = 1.5708
    c: Tangent(g3,g7) = 1.5708
    c: Tangent(g2,g7) = 1.5708
    c: Equal(g4,g7)
    c: Equal(g7,g5)
    c: Equal(g5,g6)
    c: Symmetric(g5,g4,g-2)
    c: Symmetric(g7,g6,g-2)
    c: DistanceX(g0,g0) = 50.22
    c: DistanceX(g2,g2) = 49.09
    c: DistanceY(g2,g0) = 10
    c: Radius(g4) = 3.4
    c: Coincident(g8,g0)
    c: PointOnObject(g8,g-1)
    c: Vertical(g8)
    c: Coincident(g9,g2)
    c: PointOnObject(g9,g-1)
    c: Vertical(g9)
    c: Equal(g9,g8)
FEATURE [PartDesign::Pad] Pad004
  Direction = (0,0,1)
  Length = 3.45
  Length2 = 10
  Profile = -> Sketch014
  ReferenceAxis = -> Sketch014 [N_Axis]
  Reversed = true
  Suppressed = false
  Type = 0
FEATURE [Sketcher::SketchObject] Sketch015
  ArcFitTolerance = 0
  AttachmentSupport = -> [Pad004]
  ExternalGeometry = -> [Pad004]
  FullyConstrained = true
  MakeInternals = false
  MapMode = 5
  Placement = pos=(0,0,-3.45) rot=(1,0,0;3.14159rad)
  sketch-geometry (8):
    g0: LineSegment StartX=-24.545 StartY=4.2 StartZ=0 EndX=24.545 EndY=4.2 EndZ=0
    g1: LineSegment StartX=27.1054 StartY=2.05207 StartZ=0 EndX=27.6704 EndY=-1.14793 EndZ=0
    g2: LineSegment StartX=25.11 StartY=-4.2 StartZ=0 EndX=-25.11 EndY=-4.2 EndZ=0
    g3: LineSegment StartX=-27.6704 StartY=-1.14793 StartZ=0 EndX=-27.1054 EndY=2.05207 EndZ=0
    g4: ArcOfCircle CenterX=-24.545 CenterY=1.6 CenterZ=0 NormalX=0 NormalY=0 NormalZ=1 AngleXU=0 Radius=2.6 StartAngle=1.5708 EndAngle=2.96683
    g5: ArcOfCircle CenterX=-25.11 CenterY=-1.6 CenterZ=0 NormalX=0 NormalY=0 NormalZ=1 AngleXU=0 Radius=2.6 StartAngle=2.96683 EndAngle=4.71239
    g6: ArcOfCircle CenterX=25.11 CenterY=-1.6 CenterZ=0 NormalX=0 NormalY=0 NormalZ=1 AngleXU=0 Radius=2.6 StartAngle=4.71239 EndAngle=6.45795
    g7: ArcOfCircle CenterX=24.545 CenterY=1.6 CenterZ=0 NormalX=0 NormalY=0 NormalZ=1 AngleXU=0 Radius=2.6 StartAngle=0.174761 EndAngle=1.5708
  constraints (16):
    c: Tangent(g0,g4) = 1.5708
    c: Tangent(g3,g4) = 1.5708
    c: Tangent(g3,g5) = 1.5708
    c: Tangent(g2,g5) = 1.5708
    c: Tangent(g2,g6) = 1.5708
    c: Tangent(g1,g6) = 1.5708
    c: Tangent(g1,g7) = 1.5708
    c: Tangent(g0,g7) = 1.5708
    c: Equal(g4,g5)
    c: Equal(g5,g6)
    c: Equal(g6,g7)
    c: Coincident(g4,g-3)
    c: Coincident(g7,g-5)
    c: Coincident(g-4,g5)
    c: Coincident(g6,g-6)
    c: DistanceY(g0,g-5) = 0.8
FEATURE [PartDesign::Pad] Pad005
  BaseFeature = -> Pad004
  Direction = (0,0,-1)
  Length = 2
  Length2 = 10
  Profile = -> Sketch015
  ReferenceAxis = -> Sketch015 [N_Axis]
  Suppressed = false
  Type = 0
FEATURE [PartDesign::Fillet] Fillet007
  Base = -> Pad005 [Edge4]
  BaseFeature = -> Pad005
  Radius = 0.7
  SupportTransform = false
  Suppressed = false
  UseAllEdges = false
FEATURE [Sketcher::SketchObject] Sketch016
  ArcFitTolerance = 0
  AttachmentSupport = -> [XY_Plane007]
  FullyConstrained = true
  MakeInternals = false
  MapMode = 5
  sketch-geometry (1):
    g0: Circle CenterX=0 CenterY=0 CenterZ=0 NormalX=0 NormalY=0 NormalZ=1 AngleXU=0 Radius=0.7
  constraints (2):
    c: Coincident(g0,g-1)
    c: Diameter(g0) = 1.4
FEATURE [PartDesign::Pad] Pad006
  Direction = (0,0,1)
  Length = 0.5
  Length2 = 10
  Profile = -> Sketch016
  ReferenceAxis = -> Sketch016 [N_Axis]
  Reversed = true
  Suppressed = false
  Type = 0
FEATURE [PartDesign::Body] Body007
  AllowCompound = false
  Group = -> [Sketch016,Pad006]
  Origin = -> Origin007
  Placement = pos=(-24.93,1.42,-5.45) rot=(0,0,1;0rad)
  Tip = -> Pad006
FEATURE [Part::FeaturePython] Array  # Draft array (typed FeaturePython)
  AlwaysSyncPlacement = false
  Angle = 360
  ArrayType = 0
  Axis = (0,0,1)
  Base = -> Body007
  Center = (0,0,0)
  Count = 19
  ExpandArray = false
  Fuse = false
  IntervalAxis = (0,0,0)
  IntervalX = (2.77,0,0)
  IntervalY = (0,100,0)
  IntervalZ = (0,0,100)
  NumberCircles = 3
  NumberPolar = 5
  NumberX = 19
  NumberY = 1
  NumberZ = 1
  PlacementList = 19 placements: arithmetic series from (-24.93,1.42,-5.45) step (2.77,0,0) to (24.93,1.42,-5.45)
  RadialDistance = 50
  ScaleList = (19) [(1,1,1),(1,1,1),(1,1,1),(1,1,1),(1,1,1),(1,1,1),(1,1,1),(1,1,1),(1,1,1),(1,1,1),(1,1,1),(1,1,1),(1,1,1),(1,1,1),(1,1,1),(1,1,1),(1,1,1),(1,1,1),+1 more]
  Symmetry = 1
  TangentialDistance = 25
FEATURE [Sketcher::SketchObject] Sketch017
  ArcFitTolerance = 0
  AttachmentSupport = -> [XY_Plane008]
  FullyConstrained = true
  MakeInternals = false
  MapMode = 5
  sketch-geometry (1):
    g0: Circle CenterX=0 CenterY=0 CenterZ=0 NormalX=0 NormalY=0 NormalZ=1 AngleXU=0 Radius=0.7
  constraints (2):
    c: Coincident(g0,g-1)
    c: Diameter(g0) = 1.4
FEATURE [PartDesign::Pad] Pad007
  Direction = (0,0,1)
  Length = 0.5
  Length2 = 10
  Profile = -> Sketch017
  ReferenceAxis = -> Sketch017 [N_Axis]
  Reversed = true
  Suppressed = false
  Type = 0
FEATURE [PartDesign::Body] Body008
  AllowCompound = false
  Group = -> [Sketch017,Pad007]
  Origin = -> Origin008
  Placement = pos=(-23.545,-1.42,-5.45) rot=(0,0,1;0rad)
  Tip = -> Pad007
FEATURE [Part::FeaturePython] Array001  # Draft array (typed FeaturePython)
  AlwaysSyncPlacement = false
  Angle = 360
  ArrayType = 0
  Axis = (0,0,1)
  Base = -> Body008
  Center = (0,0,0)
  Count = 18
  ExpandArray = false
  Fuse = false
  IntervalAxis = (0,0,0)
  IntervalX = (2.77,0,0)
  IntervalY = (0,100,0)
  IntervalZ = (0,0,100)
  NumberCircles = 3
  NumberPolar = 5
  NumberX = 18
  NumberY = 1
  NumberZ = 1
  PlacementList = 18 placements: arithmetic series from (-23.545,-1.42,-5.45) step (2.77,0,0) to (23.545,-1.42,-5.45)
  RadialDistance = 50
  ScaleList = (18) [(1,1,1),(1,1,1),(1,1,1),(1,1,1),(1,1,1),(1,1,1),(1,1,1),(1,1,1),(1,1,1),(1,1,1),(1,1,1),(1,1,1),(1,1,1),(1,1,1),(1,1,1),(1,1,1),(1,1,1),(1,1,1)]
  Symmetry = 1
  TangentialDistance = 25
FEATURE [Sketcher::SketchObject] Sketch019
  ArcFitTolerance = 0
  AttachmentSupport = -> [XZ_Plane010]
  FullyConstrained = true
  MakeInternals = false
  MapMode = 5
  Placement = pos=(0,0,0) rot=(1,0,0;1.5708rad)
  sketch-geometry (9):
    g0: LineSegment StartX=0 StartY=0.7 StartZ=0 EndX=-1e-16 EndY=-10.75 EndZ=0
    g1: LineSegment StartX=0.3 StartY=-10.45 StartZ=0 EndX=0.3 EndY=-2 EndZ=0
    g2: LineSegment StartX=0.3 StartY=-2 StartZ=0 EndX=0.65 EndY=-2 EndZ=0
    g3: LineSegment StartX=0.65 StartY=-2 StartZ=0 EndX=0.65 EndY=5.95 EndZ=0
    g4: ArcOfCircle CenterX=0 CenterY=-10.45 CenterZ=0 NormalX=0 NormalY=0 NormalZ=1 AngleXU=0 Radius=0.3 StartAngle=4.71239 EndAngle=6.28319
    g5: LineSegment StartX=0 StartY=0.7 StartZ=0 EndX=0.5 EndY=0.7 EndZ=0
    g6: LineSegment StartX=0.5 StartY=0.7 StartZ=0 EndX=0.5 EndY=5.8 EndZ=0
    g7: LineSegment StartX=0.5 StartY=5.8 StartZ=0 EndX=0.565 EndY=5.95 EndZ=0
    g8: LineSegment StartX=0.565 StartY=5.95 StartZ=0 EndX=0.65 EndY=5.95 EndZ=0
  constraints (27):
    c: PointOnObject(g0,g-2)
    c: PointOnObject(g0,g-2)
    c: Vertical(g1)
    c: Coincident(g1,g2)
    c: Coincident(g2,g3)
    c: Vertical(g3)
    c: PointOnObject(g4,g0)
    c: Coincident(g4,g0)
    c: Tangent(g1,g4) = -1.5708
    c: Horizontal(g2)
    c: DistanceY(g0,g-1) = 10.75
    c: DistanceY(g2,g-1) = 2
    c: DistanceX(g0,g1) = 0.3
    c: Coincident(g0,g5)
    c: Horizontal(g5)
    c: Coincident(g5,g6)
    c: Vertical(g6)
    c: Coincident(g6,g7)
    c: Coincident(g7,g8)
    c: Coincident(g8,g3)
    c: Horizontal(g8)
    c: DistanceX(g-1,g6) = 0.5
    c: DistanceX(g-1,g3) = 0.65
    c: DistanceY(g-1,g3) = 5.95
    c: DistanceY(g5,g3) = 5.25
    c: DistanceY(g6,g3) = 0.15
    c: DistanceX(g7,g7) = 0.065
FEATURE [PartDesign::Revolution] Revolution003
  Angle = 360
  Angle2 = 60
  Axis = (0,2e-16,1)
  Base = (0,0,0)
  Placement = pos=(0,0,0) rot=(1,0,0;1.5708rad)
  Profile = -> Sketch019
  ReferenceAxis = -> Sketch019 [V_Axis]
  Reversed = true
  Suppressed = false
  Type = 0
FEATURE [PartDesign::Body] Body010
  AllowCompound = false
  Group = -> [Sketch019,Revolution003]
  Origin = -> Origin010
  Placement = pos=(-23.545,-1.42,0) rot=(0,0,1;0rad)
  Tip = -> Revolution003
FEATURE [Part::FeaturePython] Array002  # Draft array (typed FeaturePython)
  AlwaysSyncPlacement = false
  Angle = 360
  ArrayType = 0
  Axis = (0,0,1)
  Base = -> Body010
  Center = (0,0,0)
  Count = 18
  ExpandArray = false
  Fuse = false
  IntervalAxis = (0,0,0)
  IntervalX = (2.77,0,0)
  IntervalY = (0,100,0)
  IntervalZ = (0,0,100)
  NumberCircles = 3
  NumberPolar = 5
  NumberX = 18
  NumberY = 1
  NumberZ = 1
  PlacementList = 18 placements: arithmetic series from (-23.545,-1.42,0) step (2.77,0,0) to (23.545,-1.42,0)
  RadialDistance = 50
  ScaleList = (18) [(1,1,1),(1,1,1),(1,1,1),(1,1,1),(1,1,1),(1,1,1),(1,1,1),(1,1,1),(1,1,1),(1,1,1),(1,1,1),(1,1,1),(1,1,1),(1,1,1),(1,1,1),(1,1,1),(1,1,1),(1,1,1)]
  Symmetry = 1
  TangentialDistance = 25
FEATURE [Part::MultiFuse] Fusion
  Shapes = -> [Array001,Array]
FEATURE [Sketcher::SketchObject] Sketch022
  ArcFitTolerance = 0
  AttachmentSupport = -> [Fillet007]
  FullyConstrained = true
  MakeInternals = false
  MapMode = 5
  sketch-geometry (10):
    g0: LineSegment StartX=-24.865 StartY=3.535 StartZ=0 EndX=24.865 EndY=3.535 EndZ=0
    g1: LineSegment StartX=26.9774 StartY=1.01766 StartZ=0 EndX=26.4874 EndY=-1.76234 EndZ=0
    g2: LineSegment StartX=24.375 StartY=-3.535 StartZ=0 EndX=-24.375 EndY=-3.535 EndZ=0
    g3: LineSegment StartX=-26.4874 StartY=-1.76234 StartZ=0 EndX=-26.9774 EndY=1.01766 EndZ=0
    g4: ArcOfCircle CenterX=-24.865 CenterY=1.39 CenterZ=0 NormalX=0 NormalY=0 NormalZ=1 AngleXU=0 Radius=2.145 StartAngle=1.5708 EndAngle=3.31606
    g5: ArcOfCircle CenterX=-24.375 CenterY=-1.39 CenterZ=0 NormalX=0 NormalY=0 NormalZ=1 AngleXU=0 Radius=2.145 StartAngle=3.31606 EndAngle=4.71239
    g6: ArcOfCircle CenterX=24.375 CenterY=-1.39 CenterZ=0 NormalX=0 NormalY=0 NormalZ=1 AngleXU=0 Radius=2.145 StartAngle=4.71239 EndAngle=6.10872
    g7: ArcOfCircle CenterX=24.865 CenterY=1.39 CenterZ=0 NormalX=0 NormalY=0 NormalZ=1 AngleXU=0 Radius=2.145 StartAngle=6.10872 EndAngle=7.85398
    g8: LineSegment [constr] StartX=-24.865 StartY=3.535 StartZ=0 EndX=-24.865 EndY=0 EndZ=0
    g9: LineSegment [constr] StartX=-24.375 StartY=-3.535 StartZ=0 EndX=-24.375 EndY=0 EndZ=0
  constraints (24):
    c: Tangent(g0,g4) = 1.5708
    c: Tangent(g3,g4) = 1.5708
    c: Tangent(g3,g5) = 1.5708
    c: Tangent(g2,g5) = 1.5708
    c: Tangent(g2,g6) = 1.5708
    c: Tangent(g1,g6) = 1.5708
    c: Tangent(g1,g7) = 1.5708
    c: Tangent(g0,g7) = 1.5708
    c: Equal(g4,g7)
    c: Equal(g7,g6)
    c: Equal(g6,g5)
    c: Coincident(g8,g0)
    c: PointOnObject(g8,g-1)
    c: Vertical(g8)
    c: Coincident(g9,g2)
    c: PointOnObject(g9,g-1)
    c: Vertical(g9)
    c: Equal(g8,g9)
    c: Symmetric(g4,g7,g-2)
    c: Symmetric(g5,g6,g-2)
    c: DistanceX(g2,g2) = 48.75
    c: DistanceX(g0,g0) = 49.73
    c: DistanceY(g2,g0) = 7.07
    c: Radius(g4) = 2.145
FEATURE [PartDesign::Pad] Pad008
  BaseFeature = -> Fillet007
  Direction = (0,0,1)
  Length = 6.55
  Length2 = 10
  Profile = -> Sketch022
  ReferenceAxis = -> Sketch022 [N_Axis]
  Suppressed = false
  Type = 0
FEATURE [PartDesign::Body] Body006
  AllowCompound = false
  Group = -> [Sketch014,Pad004,Sketch015,Pad005,Fillet007,Sketch022,Pad008]
  Origin = -> Origin006
  Tip = -> Pad008
FEATURE [Part::MultiFuse] Fusion002
  Shapes = -> [Fusion,Body006]
FEATURE [Sketcher::SketchObject] Sketch023
  ArcFitTolerance = 0
  AttachmentSupport = -> [XZ_Plane013]
  FullyConstrained = true
  MakeInternals = false
  MapMode = 5
  Placement = pos=(0,0,0) rot=(1,0,0;1.5708rad)
  sketch-geometry (9):
    g0: LineSegment StartX=0 StartY=0.7 StartZ=0 EndX=-1e-16 EndY=-10.75 EndZ=0
    g1: LineSegment StartX=0.3 StartY=-10.45 StartZ=0 EndX=0.3 EndY=-2 EndZ=0
    g2: LineSegment StartX=0.3 StartY=-2 StartZ=0 EndX=0.65 EndY=-2 EndZ=0
    g3: LineSegment StartX=0.65 StartY=-2 StartZ=0 EndX=0.65 EndY=5.95 EndZ=0
    g4: ArcOfCircle CenterX=0 CenterY=-10.45 CenterZ=0 NormalX=0 NormalY=0 NormalZ=1 AngleXU=0 Radius=0.3 StartAngle=4.71239 EndAngle=6.28319
    g5: LineSegment StartX=0 StartY=0.7 StartZ=0 EndX=0.5 EndY=0.7 EndZ=0
    g6: LineSegment StartX=0.5 StartY=0.7 StartZ=0 EndX=0.5 EndY=5.8 EndZ=0
    g7: LineSegment StartX=0.5 StartY=5.8 StartZ=0 EndX=0.565 EndY=5.95 EndZ=0
    g8: LineSegment StartX=0.565 StartY=5.95 StartZ=0 EndX=0.65 EndY=5.95 EndZ=0
  constraints (27):
    c: PointOnObject(g0,g-2)
    c: PointOnObject(g0,g-2)
    c: Vertical(g1)
    c: Coincident(g1,g2)
    c: Coincident(g2,g3)
    c: Vertical(g3)
    c: PointOnObject(g4,g0)
    c: Coincident(g4,g0)
    c: Tangent(g1,g4) = -1.5708
    c: Horizontal(g2)
    c: DistanceY(g0,g-1) = 10.75
    c: DistanceY(g2,g-1) = 2
    c: DistanceX(g0,g1) = 0.3
    c: Coincident(g0,g5)
    c: Horizontal(g5)
    c: Coincident(g5,g6)
    c: Vertical(g6)
    c: Coincident(g6,g7)
    c: Coincident(g7,g8)
    c: Coincident(g8,g3)
    c: Horizontal(g8)
    c: DistanceX(g-1,g6) = 0.5
    c: DistanceX(g-1,g3) = 0.65
    c: DistanceY(g-1,g3) = 5.95
    c: DistanceY(g5,g3) = 5.25
    c: DistanceY(g6,g3) = 0.15
    c: DistanceX(g7,g7) = 0.065
FEATURE [PartDesign::Revolution] Revolution006
  Angle = 360
  Angle2 = 60
  Axis = (0,2e-16,1)
  Base = (0,0,0)
  Placement = pos=(0,0,0) rot=(1,0,0;1.5708rad)
  Profile = -> Sketch023
  ReferenceAxis = -> Sketch023 [V_Axis]
  Reversed = true
  Suppressed = false
  Type = 0
FEATURE [PartDesign::Body] Body013
  AllowCompound = false
  Group = -> [Sketch023,Revolution006]
  Origin = -> Origin013
  Placement = pos=(-24.93,1.42,0) rot=(0,0,1;0rad)
  Tip = -> Revolution006
FEATURE [Part::FeaturePython] Array006  # Draft array (typed FeaturePython)
  AlwaysSyncPlacement = false
  Angle = 360
  ArrayType = 0
  Axis = (0,0,1)
  Base = -> Body013
  Center = (0,0,0)
  Count = 19
  ExpandArray = false
  Fuse = false
  IntervalAxis = (0,0,0)
  IntervalX = (2.77,0,0)
  IntervalY = (0,100,0)
  IntervalZ = (0,0,100)
  NumberCircles = 3
  NumberPolar = 5
  NumberX = 19
  NumberY = 1
  NumberZ = 1
  PlacementList = 19 placements: arithmetic series from (-24.93,1.42,0) step (2.77,0,0) to (24.93,1.42,0)
  RadialDistance = 50
  ScaleList = (19) [(1,1,1),(1,1,1),(1,1,1),(1,1,1),(1,1,1),(1,1,1),(1,1,1),(1,1,1),(1,1,1),(1,1,1),(1,1,1),(1,1,1),(1,1,1),(1,1,1),(1,1,1),(1,1,1),(1,1,1),(1,1,1),+1 more]
  Symmetry = 1
  TangentialDistance = 25
FEATURE [Sketcher::SketchObject] Sketch024
  ArcFitTolerance = 0
  AttachmentSupport = -> [XZ_Plane014]
  FullyConstrained = true
  MakeInternals = false
  MapMode = 5
  Placement = pos=(0,0,0) rot=(1,0,0;1.5708rad)
  sketch-geometry (7):
    g0: LineSegment StartX=0 StartY=6.65 StartZ=0 EndX=-1e-16 EndY=-10.75 EndZ=0
    g1: LineSegment StartX=0.3 StartY=-10.45 StartZ=0 EndX=0.3 EndY=-2 EndZ=0
    g2: LineSegment StartX=0.3 StartY=-2 StartZ=0 EndX=0.65 EndY=-2 EndZ=0
    g3: LineSegment StartX=0.65 StartY=-2 StartZ=0 EndX=0.65 EndY=5.95 EndZ=0
    g4: ArcOfCircle CenterX=0 CenterY=-10.45 CenterZ=0 NormalX=0 NormalY=0 NormalZ=1 AngleXU=0 Radius=0.3 StartAngle=4.71239 EndAngle=6.28319
    g5: LineSegment StartX=0.65 StartY=5.95 StartZ=0 EndX=1.35 EndY=6.65 EndZ=0
    g6: LineSegment StartX=1.35 StartY=6.65 StartZ=0 EndX=0 EndY=6.65 EndZ=0
  constraints (21):
    c: PointOnObject(g0,g-2)
    c: Vertical(g1)
    c: Coincident(g1,g2)
    c: Coincident(g2,g3)
    c: Vertical(g3)
    c: PointOnObject(g4,g0)
    c: Coincident(g4,g0)
    c: Tangent(g1,g4) = -1.5708
    c: Horizontal(g2)
    c: DistanceY(g0,g-1) = 10.75
    c: DistanceY(g2,g-1) = 2
    c: DistanceX(g0,g1) = 0.3
    c: DistanceX(g-1,g3) = 0.65
    c: DistanceY(g-1,g3) = 5.95
    c: Coincident(g3,g5)
    c: Coincident(g5,g6)
    c: Horizontal(g6)
    c: Coincident(g0,g6)
    c: PointOnObject(g0,g-2)
    c: Angle(g6,g5) = 0.785398
    c: DistanceY(g3,g0) = 0.7
FEATURE [PartDesign::Revolution] Revolution007
  Angle = 360
  Angle2 = 60
  Axis = (0,2e-16,1)
  Base = (0,0,0)
  Placement = pos=(0,0,0) rot=(1,0,0;1.5708rad)
  Profile = -> Sketch024
  ReferenceAxis = -> Sketch024 [V_Axis]
  Reversed = true
  Suppressed = false
  Type = 0
FEATURE [PartDesign::Body] Body014
  AllowCompound = false
  Group = -> [Sketch024,Revolution007]
  Origin = -> Origin014
  Placement = pos=(-23.545,-1.42,0) rot=(0,0,1;0rad)
  Tip = -> Revolution007
FEATURE [Sketcher::SketchObject] Sketch025
  ArcFitTolerance = 0
  AttachmentSupport = -> [XZ_Plane015]
  FullyConstrained = true
  MakeInternals = false
  MapMode = 5
  Placement = pos=(0,0,0) rot=(1,0,0;1.5708rad)
  sketch-geometry (7):
    g0: LineSegment StartX=0 StartY=6.65 StartZ=0 EndX=-1e-16 EndY=-10.75 EndZ=0
    g1: LineSegment StartX=0.3 StartY=-10.45 StartZ=0 EndX=0.3 EndY=-2 EndZ=0
    g2: LineSegment StartX=0.3 StartY=-2 StartZ=0 EndX=0.65 EndY=-2 EndZ=0
    g3: LineSegment StartX=0.65 StartY=-2 StartZ=0 EndX=0.65 EndY=5.95 EndZ=0
    g4: ArcOfCircle CenterX=0 CenterY=-10.45 CenterZ=0 NormalX=0 NormalY=0 NormalZ=1 AngleXU=0 Radius=0.3 StartAngle=4.71239 EndAngle=6.28319
    g5: LineSegment StartX=0.65 StartY=5.95 StartZ=0 EndX=1.35 EndY=6.65 EndZ=0
    g6: LineSegment StartX=1.35 StartY=6.65 StartZ=0 EndX=0 EndY=6.65 EndZ=0
  constraints (21):
    c: PointOnObject(g0,g-2)
    c: Vertical(g1)
    c: Coincident(g1,g2)
    c: Coincident(g2,g3)
    c: Vertical(g3)
    c: PointOnObject(g4,g0)
    c: Coincident(g4,g0)
    c: Tangent(g1,g4) = -1.5708
    c: Horizontal(g2)
    c: DistanceY(g0,g-1) = 10.75
    c: DistanceY(g2,g-1) = 2
    c: DistanceX(g0,g1) = 0.3
    c: DistanceX(g-1,g3) = 0.65
    c: DistanceY(g-1,g3) = 5.95
    c: Coincident(g3,g5)
    c: Coincident(g5,g6)
    c: Horizontal(g6)
    c: Coincident(g0,g6)
    c: PointOnObject(g0,g-2)
    c: Angle(g6,g5) = 0.785398
    c: DistanceY(g3,g0) = 0.7
FEATURE [PartDesign::Revolution] Revolution008
  Angle = 360
  Angle2 = 60
  Axis = (0,2e-16,1)
  Base = (0,0,0)
  Placement = pos=(0,0,0) rot=(1,0,0;1.5708rad)
  Profile = -> Sketch025
  ReferenceAxis = -> Sketch025 [V_Axis]
  Reversed = true
  Suppressed = false
  Type = 0
FEATURE [PartDesign::Body] Body015
  AllowCompound = false
  Group = -> [Sketch025,Revolution008]
  Origin = -> Origin015
  Placement = pos=(-24.93,1.42,0) rot=(0,0,1;0rad)
  Tip = -> Revolution008
FEATURE [Part::FeaturePython] Array007  # Draft array (typed FeaturePython)
  AlwaysSyncPlacement = false
  Angle = 360
  ArrayType = 0
  Axis = (0,0,1)
  Base = -> Body014
  Center = (0,0,0)
  Count = 36
  ExpandArray = false
  Fuse = false
  IntervalAxis = (0,0,0)
  IntervalX = (2.77,0,0)
  IntervalY = (0,100,0)
  IntervalZ = (0,0,100)
  NumberCircles = 3
  NumberPolar = 5
  NumberX = 18
  NumberY = 2
  NumberZ = 1
  PlacementList = 36 placements: [(-23.545,-1.42,0),(-23.545,98.58,0),(-20.775,-1.42,0),(-20.775,98.58,0),(-18.005,-1.42,0),(-18.005,98.58,0),(-15.235,-1.42,0),(-15.235,98.58,0),(-12.465,-1.42,0),(-12.465,98.58,0),(-9.695,-1.42,0),(-9.695,98.58,0),(-6.925,-1.42,0),(-6.925,98.58,0),(-4.155,-1.42,0),(-4.155,98.58,0),(-1.385,-1.42,0),(-1.385,98.58,0),(1.385,-1.42,0),(1.385,98.58,0),(4.155,-1.42,0),(4.155,98.58,0),(6.925,-1.42,0),+13 more]
  RadialDistance = 50
  ScaleList = (36) [(1,1,1),(1,1,1),(1,1,1),(1,1,1),(1,1,1),(1,1,1),(1,1,1),(1,1,1),(1,1,1),(1,1,1),(1,1,1),(1,1,1),(1,1,1),(1,1,1),(1,1,1),(1,1,1),(1,1,1),(1,1,1),+18 more]
  Symmetry = 1
  TangentialDistance = 25
FEATURE [Part::FeaturePython] Array008  # Draft array (typed FeaturePython)
  AlwaysSyncPlacement = false
  Angle = 360
  ArrayType = 0
  Axis = (0,0,1)
  Base = -> Body015
  Center = (0,0,0)
  Count = 19
  ExpandArray = false
  Fuse = false
  IntervalAxis = (0,0,0)
  IntervalX = (2.77,0,0)
  IntervalY = (0,100,0)
  IntervalZ = (0,0,100)
  NumberCircles = 3
  NumberPolar = 5
  NumberX = 19
  NumberY = 1
  NumberZ = 1
  PlacementList = 19 placements: arithmetic series from (-24.93,1.42,0) step (2.77,0,0) to (24.93,1.42,0)
  RadialDistance = 50
  ScaleList = (19) [(1,1,1),(1,1,1),(1,1,1),(1,1,1),(1,1,1),(1,1,1),(1,1,1),(1,1,1),(1,1,1),(1,1,1),(1,1,1),(1,1,1),(1,1,1),(1,1,1),(1,1,1),(1,1,1),(1,1,1),(1,1,1),+1 more]
  Symmetry = 1
  TangentialDistance = 25
FEATURE [Part::MultiFuse] Fusion003
  Shapes = -> [Array007,Array008]
FEATURE [Part::Cut] Cut
  Base = -> Fusion002
  Tool = -> Fusion003
